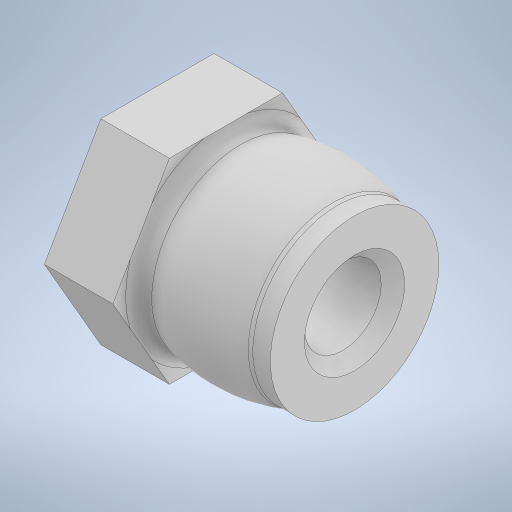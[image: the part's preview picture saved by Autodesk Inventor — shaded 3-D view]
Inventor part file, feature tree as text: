
AUTODESK INVENTOR PART (.ipt)
format: ipt  version: 2024 (Build 280153000, 153)  size: 320,000 bytes
history: native  units: in
note: dims shown in document units (in); Inventor stores cm internally (conversion verified against a paired STEP export)
features: sketch x4, extrude x3, revolve x1, fillet x1, chamfer x1, direct_edit x1, projected_geometry x1, other x1
ambient origin geometry x8: Origin, YZ Plane, XZ Plane, XY Plane, X Axis, Y Axis, Z Axis, Center Point
bodies: Solid1 (feature_tree)
feature tree (13):
  revolve  "Revolution1"  [1 undecoded]
  extrude  "Extrusion1"  Depth=0.2in
  extrude  "Extrusion2"  Depth=0.157in
  fillet  "Fillet1"  Radius=0.0174in
  chamfer  "Chamfer1"  Distance=1.0in
  direct_edit  "Direct Edit1"
  extrude  "Extrusion3"  Depth=0.3937in TaperAngle=0.0deg
  sketch  "Sketch1"  dims[d7=0.25in d8=0.098in]
  sketch  "Sketch2"  dims[d9=0.2151in d13=0.2in]
  sketch  "Sketch3"  dims[d14=0.0875in d15=0.157in d17=0.0174in]
  sketch  "Sketch4"  dims[d18=90.0deg d19=1.0in d20=0.0in d21=0.025in d22=0.0in d23=0.015in d24=0.015in d25=0.125in d26=45.0deg d27=3.937in d28=0.3937in d29=0.3937in d30=0.98in d31=1.0in d32=0.0in]
  projected_geometry  "Project Cut Edges1"
  other  "Scale1"
note: 1 required parameter value undecoded (feature->parameter linkage not recoverable at this tier; creation-order binding heuristic only, values carry confidence <= 0.55)
